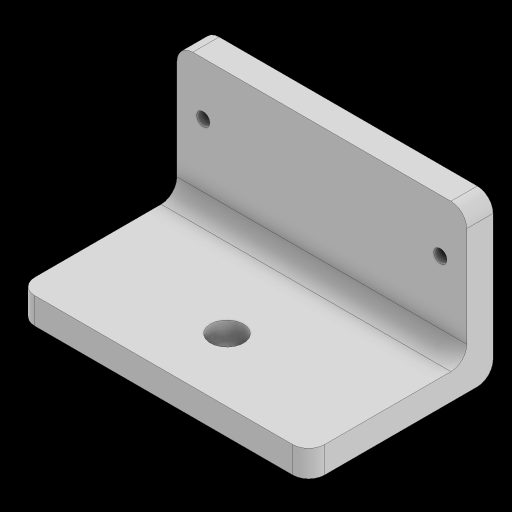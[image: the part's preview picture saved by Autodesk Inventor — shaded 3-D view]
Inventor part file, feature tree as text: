
AUTODESK INVENTOR PART (.ipt)
format: ipt  version: 2023 (Build 270158000, 158)  size: 147,968 bytes
history: native  units: mm
features: extrude x3, fillet x2, other x1, sketch x1
ambient origin geometry x8: Origin, YZ Plane, XZ Plane, XY Plane, X Axis, Y Axis, Z Axis, Center Point
bodies: Body1 (feature_tree)
feature tree (7):
  other  "ソリッド1"
  extrude  "押し出し1"  Depth=25.0mm
  extrude  "押し出し2"  Depth=55.0mm
  extrude  "押し出し3"  Depth=5.0mm
  fillet  "フィレット1"  Radius=22.5mm
  fillet  "フィレット2"  Radius=2.5mm
  sketch  "スケッチ2"
